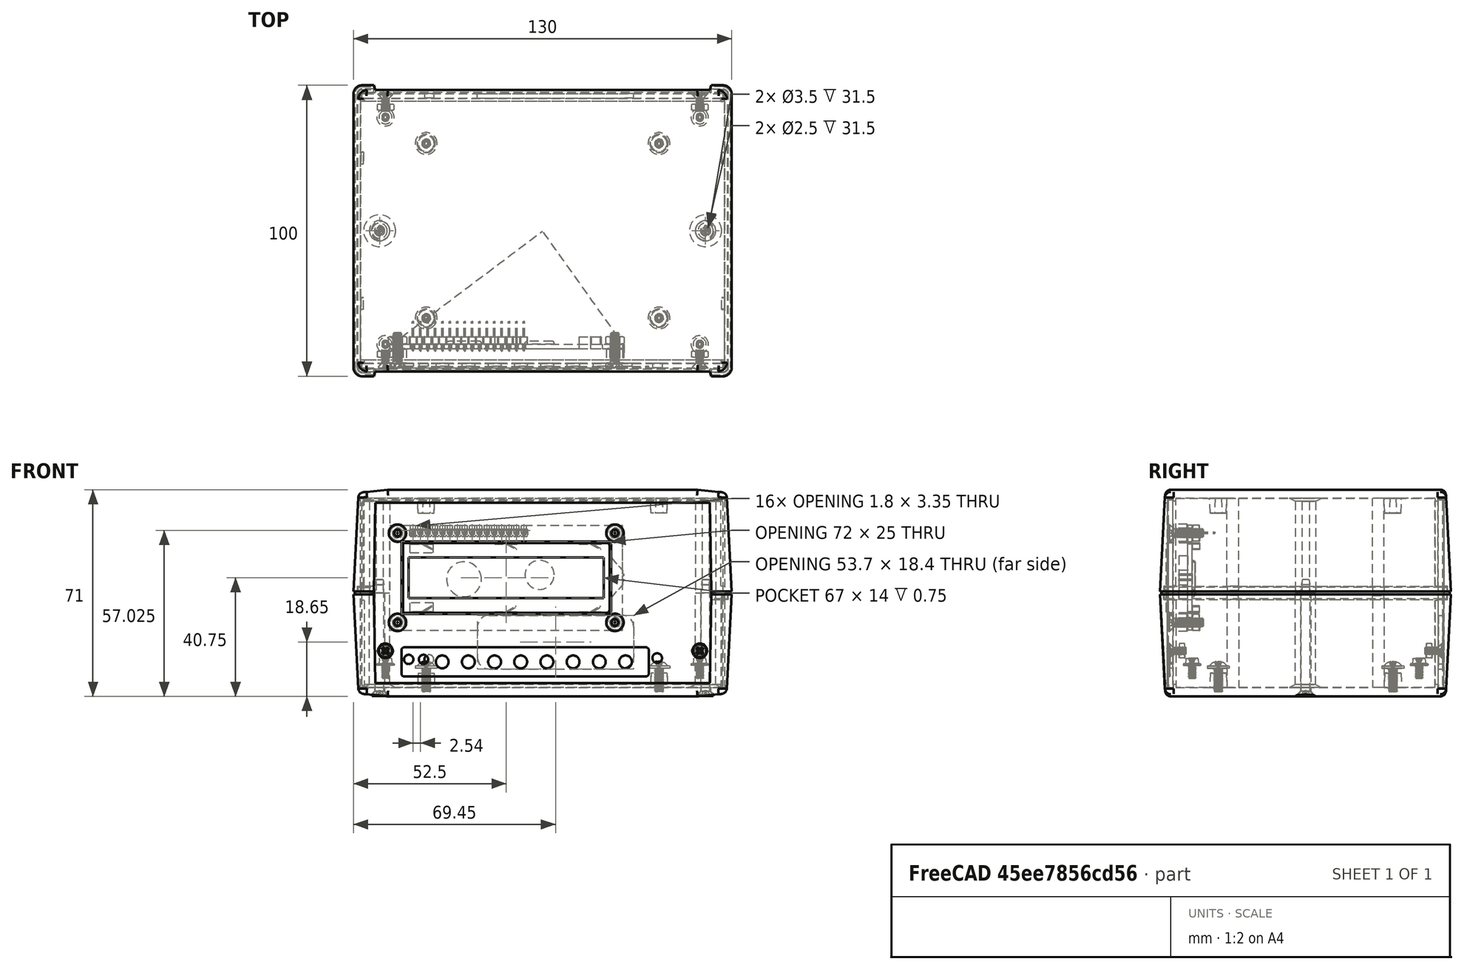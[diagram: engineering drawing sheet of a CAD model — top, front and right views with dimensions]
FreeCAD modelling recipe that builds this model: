
FCSTD DOCUMENT  (FreeCAD 0.16R6712 (Git))
Label: BBMini
License: All rights reserved
LicenseURL: http://en.wikipedia.org/wiki/All_rights_reserved
objects: Part::Feature×52, Part::Cylinder×12, App::DocumentObjectGroup×5, Part::MultiFuse×3, App::VRMLObject×2, Part::Cut×2, Part::Box×1, Part::Fillet×1
note: 71 computed .brp shape members not serialized (recipe doc carries the construction recipe); baked Part::Feature solids carry a one-line shape summary decoded from their .brp

FEATURE [Part::Feature] LCD2X16_MAIN_PART_162  label="HD44780_LCD_2x16"
  Placement = pos=(-52.5,-38.85,-13) rot=(1,0,0;1.5708rad)
  shape: bbox 80.5 x 11.4 x 36 mm, 416 faces (baked)
FEATURE [Part::Feature] Part__Feature002  label="2011LT-01A"
  Placement = pos=(0,0.1,0.25) rot=(0,0,1;0rad)
  shape: bbox 130 x 100 x 37.5 mm, 130 faces (baked)
FEATURE [Part::Feature] Part__Feature003  label="2011LB-01A"
  Placement = pos=(0,0.1,-0.75) rot=(0,1,0;3.14159rad)
  shape: bbox 130 x 100 x 37.5 mm, 138 faces (baked)
FEATURE [Part::Feature] Part__Feature005  label="Cross Recessed Flat Countersunk Head Tapping Screw - Type F - Type I - Metric M3x0.5 x 16"
  Placement = pos=(56,0.1,-35.63) rot=(0,-1,0;1.5708rad)
  shape: bbox 5.2 x 5.2 x 40 mm, 27 faces (baked)
FEATURE [Part::Feature] Part__Feature006  label="Cross Recessed Flat Countersunk Head Tapping Screw - Type F - Type I - Metric M3x0.5 x 017"
  Placement = pos=(-56,0.1,-35.63) rot=(0,-1,0;1.5708rad)
  shape: bbox 5.2 x 5.2 x 40 mm, 27 faces (baked)
FEATURE [Part::Cylinder] Cylinder004  label="LED1"
  Angle = 360
  Height = 1.8
  Placement = pos=(-45.98,-45.3,-23.05) rot=(1,0,0;1.5708rad)
  Radius = 1.6
FEATURE [Part::Cylinder] Cylinder005  label="LED2"
  Angle = 360
  Height = 1.8
  Placement = pos=(-40.9,-45.3,-23.05) rot=(1,0,0;1.5708rad)
  Radius = 1.6
FEATURE [Part::Cylinder] Cylinder006  label="Button"
  Angle = 360
  Height = 1.8
  Placement = pos=(39.38,-45.3,-22.6) rot=(1,0,0;1.5708rad)
  Radius = 1.65
FEATURE [Part::Cylinder] Cylinder007  label="TH1"
  Angle = 360
  Height = 1.8
  Placement = pos=(-34.5,-45.3,-23.9) rot=(1,0,0;1.5708rad)
  Radius = 2.2
FEATURE [Part::Cylinder] Cylinder008  label="TH2"
  Angle = 360
  Height = 1.8
  Placement = pos=(-25.5,-45.3,-23.9) rot=(1,0,0;1.5708rad)
  Radius = 2.2
FEATURE [Part::Cylinder] Cylinder009  label="TH3"
  Angle = 360
  Height = 1.8
  Placement = pos=(-16.5,-45.3,-23.9) rot=(1,0,0;1.5708rad)
  Radius = 2.2
FEATURE [Part::Cylinder] Cylinder010  label="TH4"
  Angle = 360
  Height = 1.8
  Placement = pos=(-7.5,-45.3,-23.9) rot=(1,0,0;1.5708rad)
  Radius = 2.2
FEATURE [Part::Cylinder] Cylinder011  label="TH5"
  Angle = 360
  Height = 1.8
  Placement = pos=(1.5,-45.3,-23.9) rot=(1,0,0;1.5708rad)
  Radius = 2.2
FEATURE [Part::Cylinder] Cylinder012  label="TH6"
  Angle = 360
  Height = 1.8
  Placement = pos=(10.5,-45.3,-23.9) rot=(1,0,0;1.5708rad)
  Radius = 2.2
FEATURE [Part::Cylinder] Cylinder013  label="TH7"
  Angle = 360
  Height = 1.8
  Placement = pos=(19.5,-45.3,-23.9) rot=(1,0,0;1.5708rad)
  Radius = 2.2
FEATURE [Part::Cylinder] Cylinder014  label="TH8"
  Angle = 360
  Height = 1.8
  Placement = pos=(28.5,-45.3,-23.9) rot=(1,0,0;1.5708rad)
  Radius = 2.2
FEATURE [Part::Feature] Part__Feature  label="Spacer_001"
  Placement = pos=(36.35,-40.5,15.4) rot=(1,0,0;1.5708rad)
  shape: bbox 6 x 5 x 6 mm, 8 faces (baked)
FEATURE [Part::Feature] Part__Feature007  label="Spacer_002"
  Placement = pos=(-38.35,-40.5,15.4) rot=(1,0,0;1.5708rad)
  shape: bbox 6 x 5 x 6 mm, 8 faces (baked)
FEATURE [Part::Feature] Part__Feature008  label="Spacer_003"
  Placement = pos=(36.35,-40.5,-15.4) rot=(1,0,0;1.5708rad)
  shape: bbox 6 x 5 x 6 mm, 8 faces (baked)
FEATURE [Part::Feature] Part__Feature009  label="Spacer_004"
  Placement = pos=(-38.35,-40.5,-15.4) rot=(1,0,0;1.5708rad)
  shape: bbox 6 x 5 x 6 mm, 8 faces (baked)
FEATURE [App::VRMLObject] Display  label="Display_PCB"
  Placement = pos=(-54.4,-28.4,-108.55) rot=(0,0.707107,0.707107;3.14159rad)
FEATURE [Part::Feature] Part__Feature010  label="Pin_Strip"
  Placement = pos=(-44.5,-38.75,20.5) rot=(-1,0,0;1.5708rad)
  shape: bbox 40.64 x 10.34 x 2.54 mm, 388 faces (baked)
FEATURE [Part::Cylinder] Cylinder019
  Angle = 360
  Height = 1.8
  Placement = pos=(-38.99,47.3,-23.05) rot=(1,0,0;1.5708rad)
  Radius = 1.6
FEATURE [Part::Box] Box004  label="Cube002"
  Height = 18.4
  Length = 53.7
  Placement = pos=(-22.4,45.5,-26.3) rot=(0,0,1;0rad)
  Width = 2
FEATURE [Part::Fillet] Fillet002
  Base = -> Box004
  Edges = 4 edges r=4: [Edge2,Edge4,Edge6,Edge8]
FEATURE [Part::MultiFuse] Fusion005  label="Display_Spacer"
  Placement = pos=(-11.5,0,5) rot=(0,0,1;0rad)
  Shapes = -> [Part__Feature,Part__Feature007,Part__Feature008,Part__Feature009]
FEATURE [Part::Feature] Fusion006001  label="Display_Hole_1"
  Placement = pos=(24.85,-45.5,20.35) rot=(0,0,1;0rad)
  shape: bbox 6 x 1.5 x 6 mm, 4 faces (baked)
FEATURE [Part::Feature] Fusion006002  label="Display_Hole_2"
  Placement = pos=(24.85,-45.5,-10.35) rot=(0,0,1;0rad)
  shape: bbox 6 x 1.5 x 6 mm, 4 faces (baked)
FEATURE [Part::Feature] Fusion006003  label="Display_Hole_3"
  Placement = pos=(-49.85,-45.5,20.35) rot=(0,0,1;0rad)
  shape: bbox 6 x 1.5 x 6 mm, 4 faces (baked)
FEATURE [Part::Feature] Fusion006004  label="Display_Hole_4"
  Placement = pos=(-49.85,-45.5,-10.35) rot=(0,0,1;0rad)
  shape: bbox 6 x 1.5 x 6 mm, 4 faces (baked)
FEATURE [Part::Feature] Fillet005  label="Panel_Plate"
  shape: bbox 124 x 1.5 x 64.5 mm, 10 faces (baked)
FEATURE [Part::Feature] Fillet003001  label="Display_Cut"
  shape: bbox 72 x 1.8 x 25 mm, 10 faces (baked)
FEATURE [Part::Feature] Fillet004001  label="Sink_Cut"
  shape: bbox 85 x 0.5 x 10 mm, 10 faces (baked)
FEATURE [Part::Feature] Fusion006005  label="Mounting1"
  Placement = pos=(54,0,-20.1) rot=(0,0,1;0rad)
  shape: bbox 5 x 1.5 x 5 mm, 4 faces (baked)
FEATURE [Part::Feature] Fusion006006  label="Mounting2"
  Placement = pos=(-54,0,-20.1) rot=(0,0,1;0rad)
  shape: bbox 5 x 1.5 x 5 mm, 4 faces (baked)
FEATURE [Part::MultiFuse] Fusion
  Shapes = -> [Cylinder004,Cylinder010,Cylinder011,Cylinder012,Cylinder013,Cylinder014,Cylinder005,Cylinder006,Cylinder007,Cylinder008,Cylinder009,Fusion006004,Fusion006003,Fusion006002,Fillet003001,Fusion006006,Fusion006005,Fillet004001,Fusion006001]
FEATURE [Part::Cut] Cut  label="Cut Front"
  Base = -> Fillet005
  Tool = -> Fusion
FEATURE [Part::Feature] Cut003  label="Panel Front"
  shape: bbox 124 x 1.5 x 64.5 mm, 50 faces (baked)
FEATURE [Part::Feature] ISO10642_PART_3  label="Display_Screw_001"
  Placement = pos=(-49.85,-47,20.35) rot=(1,0,0;1.5708rad)
  shape: bbox 6 x 12.44 x 6 mm, 98 faces (baked)
FEATURE [Part::Feature] ISO10642_PART_004  label="Display_Screw_002"
  Placement = pos=(-49.85,-47,-10.35) rot=(1,0,0;1.5708rad)
  shape: bbox 6 x 12.44 x 6 mm, 98 faces (baked)
FEATURE [Part::Feature] ISO10642_PART_005  label="Display_Screw_003"
  Placement = pos=(24.85,-47,20.35) rot=(1,0,0;1.5708rad)
  shape: bbox 6 x 12.44 x 6 mm, 98 faces (baked)
FEATURE [Part::Feature] ISO10642_PART_006  label="Display_Screw_004"
  Placement = pos=(24.85,-47,-10.35) rot=(1,0,0;1.5708rad)
  shape: bbox 6 x 12.44 x 6 mm, 98 faces (baked)
FEATURE [Part::Feature] ISO7047_PART_3  label="Case_001"
  Placement = pos=(54,-47,-20.1) rot=(1,0,0;1.5708rad)
  shape: bbox 4.563 x 6.935 x 4.5 mm, 66 faces (baked)
FEATURE [Part::Feature] ISO7047_PART_004  label="Case_002"
  Placement = pos=(-54,-47,-20.1) rot=(1,0,0;1.5708rad)
  shape: bbox 4.563 x 6.935 x 4.5 mm, 66 faces (baked)
FEATURE [Part::Feature] Fillet001001  label="Panel_Plate_2"
  shape: bbox 124 x 1.5 x 64.5 mm, 10 faces (baked)
FEATURE [App::DocumentObjectGroup] Group003  label="Case"
  Group = -> [Part__Feature002,Part__Feature003,Part__Feature005,Part__Feature006,XY_Plane,XZ_Plane,YZ_Plane]
FEATURE [Part::Feature] Fusion006007  label="Mounting003"
  Placement = pos=(-54,0.2,-20.1) rot=(0,0,1;3.14159rad)
  shape: bbox 5 x 1.5 x 5 mm, 4 faces (baked)
FEATURE [Part::Feature] Fusion006008  label="Mounting004"
  Placement = pos=(54,0.2,-20.1) rot=(0,0,1;3.14159rad)
  shape: bbox 5 x 1.5 x 5 mm, 4 faces (baked)
FEATURE [Part::MultiFuse] Fusion006009
  Shapes = -> [Cylinder019,Fillet002,Fusion006007,Fusion006008]
FEATURE [Part::Cut] Cut004  label="Cut Back"
  Base = -> Fillet001001
  Tool = -> Fusion006009
FEATURE [Part::Feature] Cut004001  label="Panel Back"
  shape: bbox 124 x 1.5 x 64.5 mm, 23 faces (baked)
FEATURE [App::DocumentObjectGroup] Group  label="Panel"
  Group = -> [Cut,Cut003,Cut004,Cut004001]
FEATURE [Part::Feature] ISO7047_PART_005  label="Case_003"
  Placement = pos=(54,47.2,-20.1) rot=(-1,0,0;1.5708rad)
  shape: bbox 4.563 x 6.935 x 4.5 mm, 66 faces (baked)
FEATURE [Part::Feature] ISO7047_PART_006  label="Case_004"
  Placement = pos=(-54,47.2,-20.1) rot=(-1,0,0;1.5708rad)
  shape: bbox 4.563 x 6.935 x 4.5 mm, 66 faces (baked)
FEATURE [Part::Feature] ISO4032_PART_002  label="Nut_001"
  Placement = pos=(-49.85,-36.35,20.35) rot=(1,0,0;1.5708rad)
  shape: bbox 6.351 x 3.344 x 6.351 mm, 47 faces (baked)
FEATURE [Part::Feature] ISO4032_PART_003  label="Nut_002"
  Placement = pos=(24.85,-36.35,20.35) rot=(1,0,0;1.5708rad)
  shape: bbox 6.351 x 3.344 x 6.351 mm, 47 faces (baked)
FEATURE [Part::Feature] ISO4032_PART_004  label="Nut_003"
  Placement = pos=(-49.85,-36.35,-10.35) rot=(1,0,0;1.5708rad)
  shape: bbox 6.351 x 3.344 x 6.351 mm, 47 faces (baked)
FEATURE [Part::Feature] ISO4032_PART_005  label="Nut_004"
  Placement = pos=(24.85,-36.35,-10.35) rot=(1,0,0;1.5708rad)
  shape: bbox 6.351 x 3.344 x 6.351 mm, 47 faces (baked)
FEATURE [App::DocumentObjectGroup] Group001  label="Display"
  Group = -> [Display,Part__Feature010,LCD2X16_MAIN_PART_162,Fusion005,ISO10642_PART_3,ISO10642_PART_004,ISO10642_PART_005,ISO10642_PART_006,ISO4032_PART_002,ISO4032_PART_003,ISO4032_PART_004,ISO4032_PART_005]
FEATURE [Part::Feature] ISO4032_PART_3  label="Nut_005"
  Placement = pos=(54,43.55,-20.1) rot=(1,0,0;1.5708rad)
  shape: bbox 5.774 x 2.897 x 5.774 mm, 46 faces (baked)
FEATURE [Part::Feature] ISO4032_PART_006  label="Nut_006"
  Placement = pos=(-54,-41.35,-20.1) rot=(1,0,0;1.5708rad)
  shape: bbox 5.774 x 2.897 x 5.774 mm, 46 faces (baked)
FEATURE [Part::Feature] ISO4032_PART_008  label="Nut_008"
  Placement = pos=(54,-41.35,-20.1) rot=(1,0,0;1.5708rad)
  shape: bbox 5.774 x 2.897 x 5.774 mm, 46 faces (baked)
FEATURE [Part::Feature] ISO4032_PART_009  label="Nut_009"
  Placement = pos=(-54,43.55,-20.1) rot=(1,0,0;1.5708rad)
  shape: bbox 5.774 x 2.897 x 5.774 mm, 46 faces (baked)
FEATURE [App::DocumentObjectGroup] Group002  label="Screws & Nuts"
  Group = -> [ISO7047_PART_3,ISO7047_PART_004,ISO7047_PART_005,ISO7047_PART_006,ISO4032_PART_3,ISO4032_PART_006,ISO4032_PART_008,ISO4032_PART_009]
FEATURE [Part::Feature] ISO7048_PART_1  label="Screw_001"
  Placement = pos=(54,39.1,-24.49) rot=(0,0,1;0rad)
  shape: bbox 4.563 x 4.5 x 7.25 mm, 74 faces (baked)
FEATURE [Part::Feature] ISO7089_PART_1  label="Nut_011"
  Placement = pos=(54,39.1,-25.1) rot=(0,0,1;0rad)
  shape: bbox 6 x 6 x 0.55 mm, 4 faces (baked)
FEATURE [Part::Feature] ISO7048_PART_002  label="Screw_002"
  Placement = pos=(-54,39.1,-24.49) rot=(0,0,1;0rad)
  shape: bbox 4.563 x 4.5 x 7.25 mm, 74 faces (baked)
FEATURE [Part::Feature] ISO7089_PART_002  label="Nut_012"
  Placement = pos=(-54,39.1,-25.1) rot=(0,0,1;0rad)
  shape: bbox 6 x 6 x 0.55 mm, 4 faces (baked)
FEATURE [Part::Feature] ISO7048_PART_003  label="Screw_003"
  Placement = pos=(54,-38.9,-24.49) rot=(0,0,1;0rad)
  shape: bbox 4.563 x 4.5 x 7.25 mm, 74 faces (baked)
FEATURE [Part::Feature] ISO7089_PART_003  label="Nut_013"
  Placement = pos=(54,-38.9,-25.1) rot=(0,0,1;0rad)
  shape: bbox 6 x 6 x 0.55 mm, 4 faces (baked)
FEATURE [Part::Feature] ISO7048_PART_004  label="Screw_004"
  Placement = pos=(-54,-38.9,-24.49) rot=(0,0,1;0rad)
  shape: bbox 4.563 x 4.5 x 7.25 mm, 74 faces (baked)
FEATURE [Part::Feature] ISO7089_PART_004  label="Nut_014"
  Placement = pos=(-54,-38.9,-25.1) rot=(0,0,1;0rad)
  shape: bbox 6 x 6 x 0.55 mm, 4 faces (baked)
FEATURE [Part::Feature] DIN967_PART_1  label="Nut_015"
  Placement = pos=(40,30.1,-26.1) rot=(0,0,1;0rad)
  shape: bbox 7.5 x 7.5 x 10.79 mm, 94 faces (baked)
FEATURE [Part::Feature] DIN967_PART_002  label="Nut_016"
  Placement = pos=(40,-29.9,-26.1) rot=(0,0,1;0rad)
  shape: bbox 7.5 x 7.5 x 10.79 mm, 94 faces (baked)
FEATURE [Part::Feature] DIN967_PART_003  label="Nut_017"
  Placement = pos=(-40,30.1,-26.1) rot=(0,0,1;0rad)
  shape: bbox 7.5 x 7.5 x 10.79 mm, 94 faces (baked)
FEATURE [Part::Feature] DIN967_PART_004  label="Nut_018"
  Placement = pos=(-40,-29.9,-26.1) rot=(0,0,1;0rad)
  shape: bbox 7.5 x 7.5 x 10.79 mm, 94 faces (baked)
FEATURE [App::VRMLObject] BBMini001  label="BBMini"
  Placement = pos=(-61.48,-45.4,-26.95) rot=(0,0,1;0rad)
FEATURE [App::DocumentObjectGroup] Group004  label="PCB"
  Group = -> [ISO7048_PART_1,ISO7089_PART_1,ISO7048_PART_002,ISO7089_PART_002,ISO7048_PART_003,ISO7089_PART_003,ISO7048_PART_004,ISO7089_PART_004,DIN967_PART_1,DIN967_PART_002,DIN967_PART_003,DIN967_PART_004,BBMini001]
